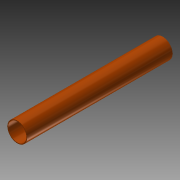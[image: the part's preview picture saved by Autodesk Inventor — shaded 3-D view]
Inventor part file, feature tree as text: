
AUTODESK INVENTOR PART (.ipt)
format: ipt  version: 2015 (Build 190159000, 159)  size: 77,824 bytes
history: native  units: in
note: dims shown in document units (in); Inventor stores cm internally (conversion verified against a paired STEP export)
features: extrude x1, sketch x1
ambient origin geometry x8: Origin, YZ Plane, XZ Plane, XY Plane, X Axis, Y Axis, Z Axis, Center Point
bodies: Solid1 (feature_tree)
feature tree (2):
  extrude  "Extrusion1"  Depth=41.375in
  sketch  "Sketch1"  dims[d0=5.625in d1=5.188in d2=41.375in d3=0.0in]
